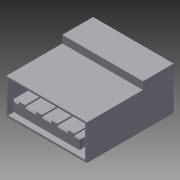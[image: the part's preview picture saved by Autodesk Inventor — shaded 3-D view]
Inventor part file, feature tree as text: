
AUTODESK INVENTOR PART (.ipt)
format: ipt  version: 2012 (Build 160160000, 160)  size: 157,184 bytes
history: native  units: mm
features: chamfer x6, extrude x3, sketch x3, fillet x2
ambient origin geometry x8: Origin, YZ Plane, XZ Plane, XY Plane, X Axis, Y Axis, Z Axis, Center Point
bodies: Solid1 (feature_tree)
feature tree (14):
  extrude  "Extrusion1"  Depth=14.1mm
  extrude  "Extrusion2"  Depth=5.0mm
  extrude  "Extrusion3"  Depth=0.3mm
  fillet  "Fillet3"  Radius=5.72mm
  fillet  "Fillet4"  Radius=5.12mm
  chamfer  "Chamfer1"  Distance=0.7mm
  chamfer  "Chamfer2"  Distance=1.84mm
  chamfer  "Chamfer3"  Distance=0.7mm
  chamfer  "Chamfer4"  Distance=10.3mm
  chamfer  "Chamfer5"  Distance=2.56mm
  chamfer  "Chamfer6"  Distance=1.0mm
  sketch  "Sketch1"  dims[d0=13.1mm d1=14.1mm]
  sketch  "Sketch2"  dims[d2=5.72mm d3=0.0mm d4=5.0mm]
  sketch  "Sketch3"  dims[d5=1.23mm d6=0.0mm d7=0.3mm d9=5.72mm d10=5.12mm d11=0.7mm d13=1.84mm d14=0.7mm d15=10.3mm d16=0.0mm d17=2.56mm d20=1.0mm d21=0.25mm d22=1.0mm d23=1.0mm d24=1.0mm d25=0.25mm d26=0.25mm d27=0.25mm d28=1.05mm d29=1.75mm d30=1.5mm d31=1.75mm d32=0.64mm d33=0.64mm d34=0.2mm d35=5.0mm d36=45.0deg d37=0.2mm d38=5.0mm d39=45.0deg d40=0.2mm d41=5.0mm d42=45.0deg d43=0.2mm d44=5.0mm d45=45.0deg d46=0.2mm d47=5.0mm d48=45.0deg d49=0.2mm d50=5.0mm d51=45.0deg]
